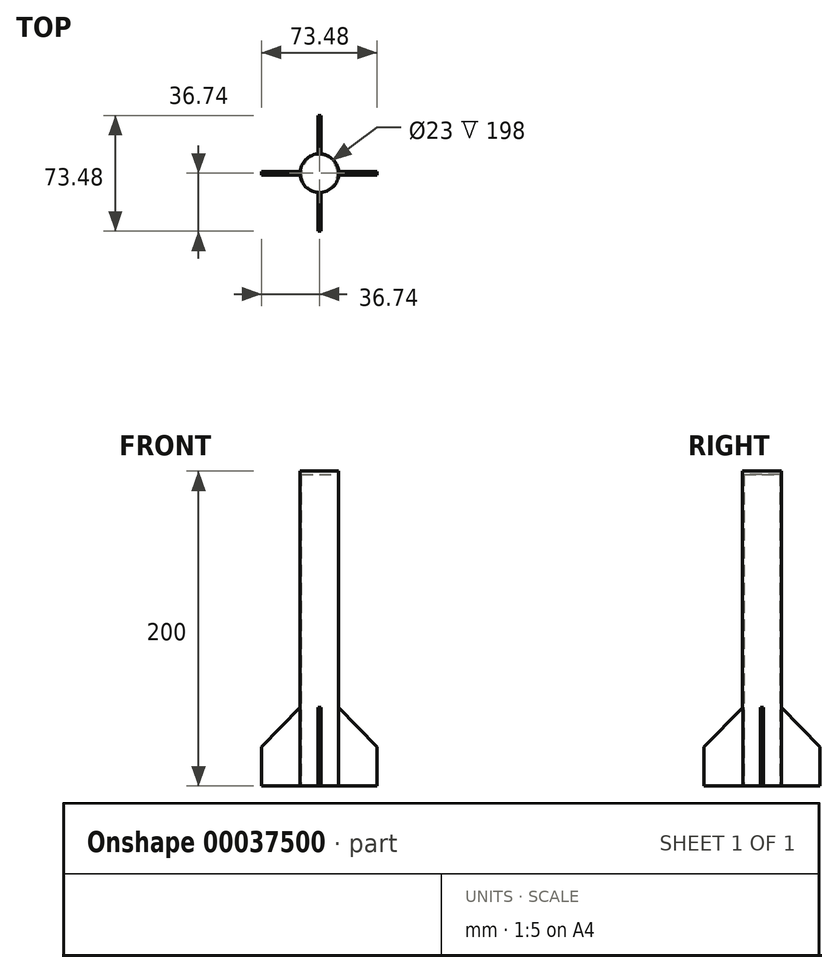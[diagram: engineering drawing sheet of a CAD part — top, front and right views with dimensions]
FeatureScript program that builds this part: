
annotation { "Feature Type Name" : "Feature", "Feature Type Description" : "" }
export const myFeature = defineFeature(function(context is Context, id is Id, definition is map)
    precondition{}
    {
        {
            var Q0;
            Q0=qCreatedBy(makeId("Front.planeOp"),FACE);
            var sketch = newSketch(context, id + "F0", { "sketchPlane" : qUnion([Q0])});
            skLineSegment(sketch, "E0", {"start": v(-11.5, 0) * mm, "end": v(-12.3, 0) * mm});
            skLineSegment(sketch, "E1", {"start": v(-12.3, 0) * mm, "end": v(-12.3, 200) * mm});
            skLineSegment(sketch, "E2", {"start": v(-11.5, 0) * mm, "end": v(-11.5, 198) * mm});
            skLineSegment(sketch, "E3", {"start": v(0, -35.22) * mm, "end": v(0, 226.09) * mm});
            skLineSegment(sketch, "E4", {"start": v(-12.3, 200) * mm, "end": v(0, 200) * mm});
            skLineSegment(sketch, "E5", {"start": v(-11.5, 198) * mm, "end": v(0, 198) * mm});
            skLineSegment(sketch, "E6", {"start": v(0, 198) * mm, "end": v(0, 200) * mm});
            skSolve(sketch);
        }
        {
            var Q0;
            Q0=makeQuery(id+"F0.imprint","IMPRINT",FACE,{"disambiguationData":[TD([[makeQuery(id+"F0.imprint","IMPRINT",EDGE,{"derivedFrom":sQuery(id+"F0.wireOp",EDGE,"E0")}),-1.0]])]});
            var Q1;
            Q1=sQuery(id+"F0.wireOp",EDGE,"E3");
            revolve(context, id + "F1", {"entities" : qUnion([Q0]), "axis" : qUnion([Q1]), "revolveType" : RevolveType.FULL});
        }
        {
            var Q0;
            Q0=qCreatedBy(makeId("Right.planeOp"),FACE);
            var sketch = newSketch(context, id + "F2", { "sketchPlane" : qUnion([Q0])});
            skLineSegment(sketch, "E7", {"start": v(-11.74, 0) * mm, "end": v(-36.74, 0) * mm});
            skLineSegment(sketch, "E8", {"start": v(-36.74, 0) * mm, "end": v(-36.74, 25) * mm});
            skLineSegment(sketch, "E9", {"start": v(-36.74, 25) * mm, "end": v(-12.25, 50.06) * mm});
            skLineSegment(sketch, "E10", {"start": v(-12.25, 50.06) * mm, "end": v(-11.74, 0) * mm});
            skSolve(sketch);
        }
        {
            var Q0;
            Q0=makeQuery(id+"F2.imprint","IMPRINT",FACE,{"disambiguationData":[TD([[makeQuery(id+"F2.imprint","IMPRINT",EDGE,{"derivedFrom":sQuery(id+"F2.wireOp",EDGE,"E7")}),-1.0]])]});
            extrude(context, id + "F3", {"entities" : qUnion([Q0]), "endBound" : BoundingType.SYMMETRIC, "depth" : 2 * mm});
        }
        {
            var Q0;
            Q0=makeQuery(id+"F3.opExtrude","SWEPT_BODY",BODY,{"disambiguationData":[OSD([sQuery(id+"F2.wireOp",EDGE,"E7"),sQuery(id+"F2.wireOp",EDGE,"E8"),sQuery(id+"F2.wireOp",EDGE,"E9"),sQuery(id+"F2.wireOp",EDGE,"E10")])]});
            var Q1;
            Q1=makeQuery(id+"F1.opRevolve","SWEPT_FACE",FACE,{"disambiguationData":[OSD([sQuery(id+"F0.wireOp",EDGE,"E1")])]});
            circularPattern(context, id + "F4", {"operationType" : NewBodyOperationType.ADD, "entities" : qUnion([Q0]), "axis" : qUnion([Q1]), "angle" : 360 * degree, "instanceCount" : 4, "equalSpace" : true});
        }
    });
